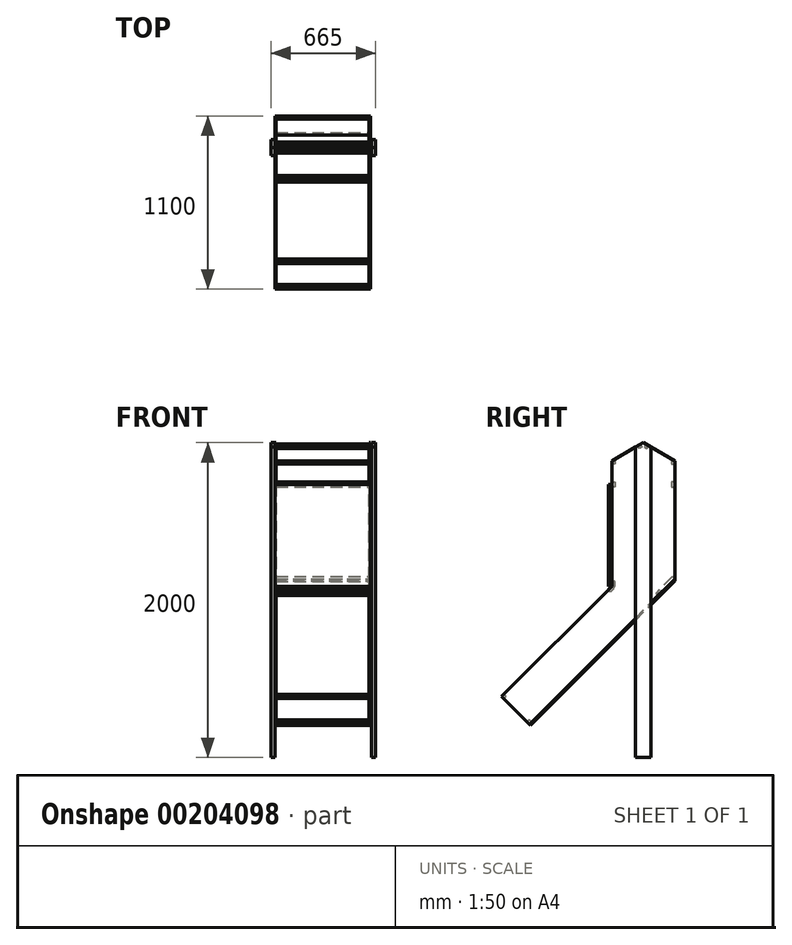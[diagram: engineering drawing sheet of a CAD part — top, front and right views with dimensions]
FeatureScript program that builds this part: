
annotation { "Feature Type Name" : "Feature", "Feature Type Description" : "" }
export const myFeature = defineFeature(function(context is Context, id is Id, definition is map)
    precondition{}
    {
        {
            var Q0;
            Q0=qCreatedBy(makeId("Right.planeOp"),FACE);
            var sketch = newSketch(context, id + "F0", { "sketchPlane" : qUnion([Q0])});
            skLineSegment(sketch, "E0", {"start": v(-408.2, -388.22) * mm, "end": v(515.03, 535) * mm});
            skLineSegment(sketch, "E1", {"start": v(515.03, 535) * mm, "end": v(515.03, 1285) * mm});
            skLineSegment(sketch, "E2", {"start": v(115.03, 1285) * mm, "end": v(115.03, 488.55) * mm});
            skLineSegment(sketch, "E3", {"start": v(115.03, 488.55) * mm, "end": v(-584.97, -211.45) * mm});
            skLineSegment(sketch, "E4", {"start": v(115.03, 1285) * mm, "end": v(315.03, 1400.47) * mm});
            skLineSegment(sketch, "E5", {"start": v(315.03, 1400.47) * mm, "end": v(515.03, 1285) * mm});
            skLineSegment(sketch, "E6", {"start": v(-408.2, -388.22) * mm, "end": v(-584.97, -211.45) * mm});
            skPoint(sketch, "E7.orphan", {"position": v(-373.53, 0) * mm});
            skSolve(sketch);
        }
        {
            var Q0;
            Q0=makeQuery(id+"F0.imprint","IMPRINT",FACE,{"disambiguationData":[TD([[makeQuery(id+"F0.imprint","IMPRINT",EDGE,{"derivedFrom":sQuery(id+"F0.wireOp",EDGE,"E0")}),1.0]])]});
            extrude(context, id + "F1", {"entities" : qUnion([Q0]), "depth" : 9 * mm});
        }
        {
            var Q0;
            Q0=makeQuery(id+"F1.opExtrude","SWEPT_BODY",BODY,{"disambiguationData":[OSD([sQuery(id+"F0.wireOp",EDGE,"E0"),sQuery(id+"F0.wireOp",EDGE,"E1"),sQuery(id+"F0.wireOp",EDGE,"E2"),sQuery(id+"F0.wireOp",EDGE,"E3"),sQuery(id+"F0.wireOp",EDGE,"E4"),sQuery(id+"F0.wireOp",EDGE,"E5"),sQuery(id+"F0.wireOp",EDGE,"E6")])]});
            transform(context, id + "F2", {"entities" : qUnion([Q0]), "transformType" : TransformType.TRANSLATION_3D, "dx" : 600 * mm, "dy" : 0 * mm, "dz" : 0 * mm, "makeCopy" : true});
        }
        {
            var Q0;
            Q0=makeQuery(id+"F2.opPattern","COPY",FACE,{"derivedFrom":makeQuery(id+"F1.opExtrude","CAP_FACE",FACE,{"disambiguationData":[OSD([sQuery(id+"F0.wireOp",EDGE,"E0"),sQuery(id+"F0.wireOp",EDGE,"E1"),sQuery(id+"F0.wireOp",EDGE,"E2"),sQuery(id+"F0.wireOp",EDGE,"E3"),sQuery(id+"F0.wireOp",EDGE,"E4"),sQuery(id+"F0.wireOp",EDGE,"E5"),sQuery(id+"F0.wireOp",EDGE,"E6")])],"isStart":true}),"instanceName":"1"});
            var sketch = newSketch(context, id + "F3", { "sketchPlane" : qUnion([Q0])});
            skLineSegment(sketch, "E8", {"start": v(-515.03, 535) * mm, "end": v(-408.96, 428.93) * mm});
            skLineSegment(sketch, "E9", {"start": v(-408.96, 428.93) * mm, "end": v(-394.82, 443.08) * mm});
            skLineSegment(sketch, "E10", {"start": v(-394.82, 443.08) * mm, "end": v(-500.89, 549.14) * mm});
            skLineSegment(sketch, "E11", {"start": v(-500.89, 549.14) * mm, "end": v(-515.03, 535) * mm});
            skLineSegment(sketch, "E12", {"start": v(408.2, -388.22) * mm, "end": v(422.34, -374.08) * mm});
            skLineSegment(sketch, "E13", {"start": v(422.34, -374.08) * mm, "end": v(408.2, -359.94) * mm});
            skLineSegment(sketch, "E14", {"start": v(408.2, -359.94) * mm, "end": v(394.05, -374.08) * mm});
            skLineSegment(sketch, "E15", {"start": v(394.05, -374.08) * mm, "end": v(408.2, -388.22) * mm});
            skLineSegment(sketch, "E16", {"start": v(584.97, -211.45) * mm, "end": v(570.83, -225.59) * mm});
            skLineSegment(sketch, "E17", {"start": v(570.83, -225.59) * mm, "end": v(556.69, -211.45) * mm});
            skLineSegment(sketch, "E18", {"start": v(556.69, -211.45) * mm, "end": v(570.83, -197.3) * mm});
            skLineSegment(sketch, "E19", {"start": v(570.83, -197.3) * mm, "end": v(584.97, -211.45) * mm});
            skLineSegment(sketch, "E20", {"start": v(-515.03, 1285) * mm, "end": v(-515.03, 1265) * mm});
            skLineSegment(sketch, "E21", {"start": v(-515.03, 1265) * mm, "end": v(-495.03, 1265) * mm});
            skLineSegment(sketch, "E22", {"start": v(-495.03, 1265) * mm, "end": v(-495.03, 1285) * mm});
            skLineSegment(sketch, "E23", {"start": v(-495.03, 1285) * mm, "end": v(-515.03, 1285) * mm});
            skLineSegment(sketch, "E24", {"start": v(-115.03, 1285) * mm, "end": v(-115.03, 1265) * mm});
            skLineSegment(sketch, "E25", {"start": v(-115.03, 1265) * mm, "end": v(-135.03, 1265) * mm});
            skLineSegment(sketch, "E26", {"start": v(-135.03, 1265) * mm, "end": v(-135.03, 1285) * mm});
            skLineSegment(sketch, "E27", {"start": v(-135.03, 1285) * mm, "end": v(-115.03, 1285) * mm});
            skLineSegment(sketch, "E28", {"start": v(-332.35, 1390.47) * mm, "end": v(-349.67, 1380.47) * mm});
            skLineSegment(sketch, "E29", {"start": v(-349.67, 1380.47) * mm, "end": v(-339.67, 1363.15) * mm});
            skLineSegment(sketch, "E30", {"start": v(-339.67, 1363.15) * mm, "end": v(-322.35, 1373.15) * mm});
            skLineSegment(sketch, "E31", {"start": v(-322.35, 1373.15) * mm, "end": v(-332.35, 1390.47) * mm});
            skPoint(sketch, "E32.orphan", {"position": v(-332, 1389.88) * mm});
            skPoint(sketch, "E33.orphan", {"position": v(-332, 1390.67) * mm});
            skLineSegment(sketch, "E34", {"start": v(-297.7, 1390.47) * mm, "end": v(-280.39, 1380.47) * mm});
            skLineSegment(sketch, "E35", {"start": v(-280.39, 1380.47) * mm, "end": v(-290.39, 1363.15) * mm});
            skLineSegment(sketch, "E36", {"start": v(-290.39, 1363.15) * mm, "end": v(-307.7, 1373.15) * mm});
            skLineSegment(sketch, "E37", {"start": v(-307.7, 1373.15) * mm, "end": v(-297.7, 1390.47) * mm});
            skPoint(sketch, "E38.orphan", {"position": v(-298.36, 1389.35) * mm});
            skPoint(sketch, "E39.orphan", {"position": v(-295.76, 1389.35) * mm});
            skLineSegment(sketch, "E40", {"start": v(-115.03, 488.55) * mm, "end": v(-93.81, 467.34) * mm});
            skLineSegment(sketch, "E41", {"start": v(-93.81, 467.34) * mm, "end": v(-107.96, 453.2) * mm});
            skLineSegment(sketch, "E42", {"start": v(-107.96, 453.2) * mm, "end": v(-129.17, 474.41) * mm});
            skPoint(sketch, "E43.orphan", {"position": v(-115.03, 562.54) * mm});
            skLineSegment(sketch, "E44", {"start": v(-115.03, 488.55) * mm, "end": v(-129.17, 474.41) * mm});
            skLineSegment(sketch, "E45", {"start": v(-115.03, 488.55) * mm, "end": v(-115.03, 518.55) * mm});
            skLineSegment(sketch, "E46", {"start": v(-115.03, 518.55) * mm, "end": v(-135.03, 518.55) * mm});
            skLineSegment(sketch, "E47", {"start": v(-135.03, 518.55) * mm, "end": v(-135.03, 488.55) * mm});
            skLineSegment(sketch, "E48", {"start": v(-135.03, 488.55) * mm, "end": v(-115.03, 488.55) * mm});
            skLineSegment(sketch, "E49", {"start": v(-115.03, 1150) * mm, "end": v(-115.03, 1120) * mm});
            skLineSegment(sketch, "E50", {"start": v(-115.03, 1120) * mm, "end": v(-135.03, 1120) * mm});
            skLineSegment(sketch, "E51", {"start": v(-135.03, 1120) * mm, "end": v(-135.03, 1150) * mm});
            skLineSegment(sketch, "E52", {"start": v(-135.03, 1150) * mm, "end": v(-115.03, 1150) * mm});
            skLineSegment(sketch, "E53", {"start": v(-515.03, 1150) * mm, "end": v(-515.03, 1120) * mm});
            skLineSegment(sketch, "E54", {"start": v(-515.03, 1120) * mm, "end": v(-495.03, 1120) * mm});
            skLineSegment(sketch, "E55", {"start": v(-495.03, 1120) * mm, "end": v(-495.03, 1150) * mm});
            skLineSegment(sketch, "E56", {"start": v(-495.03, 1150) * mm, "end": v(-515.03, 1150) * mm});
            skPoint(sketch, "E57.orphan", {"position": v(-515.03, 1099.84) * mm});
            skSolve(sketch);
        }
        {
            var Q0;
            Q0 = qSketchRegion(id + "F3", true);
            extrude(context, id + "F4", {"entities" : qUnion([Q0]), "endBound" : BoundingType.UP_TO_NEXT, "depth" : 25 * mm});
        }
        {
            var Q0;
            Q0=makeQuery(id+"F4.opExtrude","SWEPT_FACE",FACE,{"disambiguationData":[OSD([sQuery(id+"F3.wireOp",EDGE,"E45")])]});
            var sketch = newSketch(context, id + "F5", { "sketchPlane" : qUnion([Q0])});
            skLineSegment(sketch, "E58", {"start": v(0, 488.55) * mm, "end": v(609, 488.55) * mm});
            skLineSegment(sketch, "E59", {"start": v(609, 488.55) * mm, "end": v(609, 1133.58) * mm});
            skLineSegment(sketch, "E60", {"start": v(609, 1133.58) * mm, "end": v(0, 1133.58) * mm});
            skLineSegment(sketch, "E61", {"start": v(0, 1133.58) * mm, "end": v(0, 488.55) * mm});
            skSolve(sketch);
        }
        {
            var Q0;
            Q0 = qSketchRegion(id + "F5", true);
            extrude(context, id + "F6", {"entities" : qUnion([Q0]), "depth" : 20 * mm});
        }
        {
            var Q0;
            Q0=makeQuery(id+"F2.opPattern","COPY",FACE,{"derivedFrom":makeQuery(id+"F1.opExtrude","CAP_FACE",FACE,{"disambiguationData":[OSD([sQuery(id+"F0.wireOp",EDGE,"E0"),sQuery(id+"F0.wireOp",EDGE,"E1"),sQuery(id+"F0.wireOp",EDGE,"E2"),sQuery(id+"F0.wireOp",EDGE,"E3"),sQuery(id+"F0.wireOp",EDGE,"E4"),sQuery(id+"F0.wireOp",EDGE,"E5"),sQuery(id+"F0.wireOp",EDGE,"E6")])],"isStart":false}),"instanceName":"1"});
            var sketch = newSketch(context, id + "F7", { "sketchPlane" : qUnion([Q0])});
            skLineSegment(sketch, "E62", {"start": v(515.03, 535) * mm, "end": v(-408.2, -388.22) * mm});
            skLineSegment(sketch, "E63", {"start": v(-408.2, -388.22) * mm, "end": v(-401.13, -395.3) * mm});
            skLineSegment(sketch, "E64", {"start": v(-401.13, -395.3) * mm, "end": v(515.03, 520.86) * mm});
            skLineSegment(sketch, "E65", {"start": v(515.03, 535) * mm, "end": v(515.03, 520.86) * mm});
            skSolve(sketch);
        }
        {
            var Q0;
            Q0 = qSketchRegion(id + "F7", true);
            var Q1;
            Q1=makeQuery(id+"F1.opExtrude","CAP_FACE",FACE,{"disambiguationData":[OSD([sQuery(id+"F0.wireOp",EDGE,"E0"),sQuery(id+"F0.wireOp",EDGE,"E1"),sQuery(id+"F0.wireOp",EDGE,"E2"),sQuery(id+"F0.wireOp",EDGE,"E3"),sQuery(id+"F0.wireOp",EDGE,"E4"),sQuery(id+"F0.wireOp",EDGE,"E5"),sQuery(id+"F0.wireOp",EDGE,"E6")])],"isStart":true});
            extrude(context, id + "F8", {"entities" : qUnion([Q0]), "endBound" : BoundingType.UP_TO_SURFACE, "oppositeDirection" : true, "endBoundEntityFace" : qUnion([Q1]), "depth" : 25 * mm});
        }
        {
            var Q0;
            Q0=makeQuery(id+"F1.opExtrude","CAP_FACE",FACE,{"disambiguationData":[OSD([sQuery(id+"F0.wireOp",EDGE,"E0"),sQuery(id+"F0.wireOp",EDGE,"E1"),sQuery(id+"F0.wireOp",EDGE,"E2"),sQuery(id+"F0.wireOp",EDGE,"E3"),sQuery(id+"F0.wireOp",EDGE,"E4"),sQuery(id+"F0.wireOp",EDGE,"E5"),sQuery(id+"F0.wireOp",EDGE,"E6")])],"isStart":true});
            var sketch = newSketch(context, id + "F9", { "sketchPlane" : qUnion([Q0])});
            skLineSegment(sketch, "E66", {"start": v(-315.03, 1400.47) * mm, "end": v(-365.03, 1371.6) * mm});
            skLineSegment(sketch, "E67", {"start": v(-365.03, 1371.6) * mm, "end": v(-365.03, -599.53) * mm});
            skLineSegment(sketch, "E68", {"start": v(-365.03, -599.53) * mm, "end": v(-265.03, -599.53) * mm});
            skLineSegment(sketch, "E69", {"start": v(-265.03, -599.53) * mm, "end": v(-265.03, 1371.6) * mm});
            skLineSegment(sketch, "E70", {"start": v(-265.03, 1371.6) * mm, "end": v(-315.03, 1400.47) * mm});
            skSolve(sketch);
        }
        {
            var Q0;
            Q0 = qSketchRegion(id + "F9", true);
            extrude(context, id + "F10", {"entities" : qUnion([Q0]), "depth" : 25 * mm});
        }
        {
            var Q0;
            Q0=makeQuery(id+"F10.opExtrude","SWEPT_BODY",BODY,{"disambiguationData":[OSD([sQuery(id+"F9.wireOp",EDGE,"E66"),sQuery(id+"F9.wireOp",EDGE,"E67"),sQuery(id+"F9.wireOp",EDGE,"E68"),sQuery(id+"F9.wireOp",EDGE,"E69"),sQuery(id+"F9.wireOp",EDGE,"E70")])]});
            transform(context, id + "F11", {"entities" : qUnion([Q0]), "transformType" : TransformType.TRANSLATION_3D, "dx" : 640 * mm, "dy" : 0 * mm, "dz" : 0 * mm, "makeCopy" : true});
        }
    });
